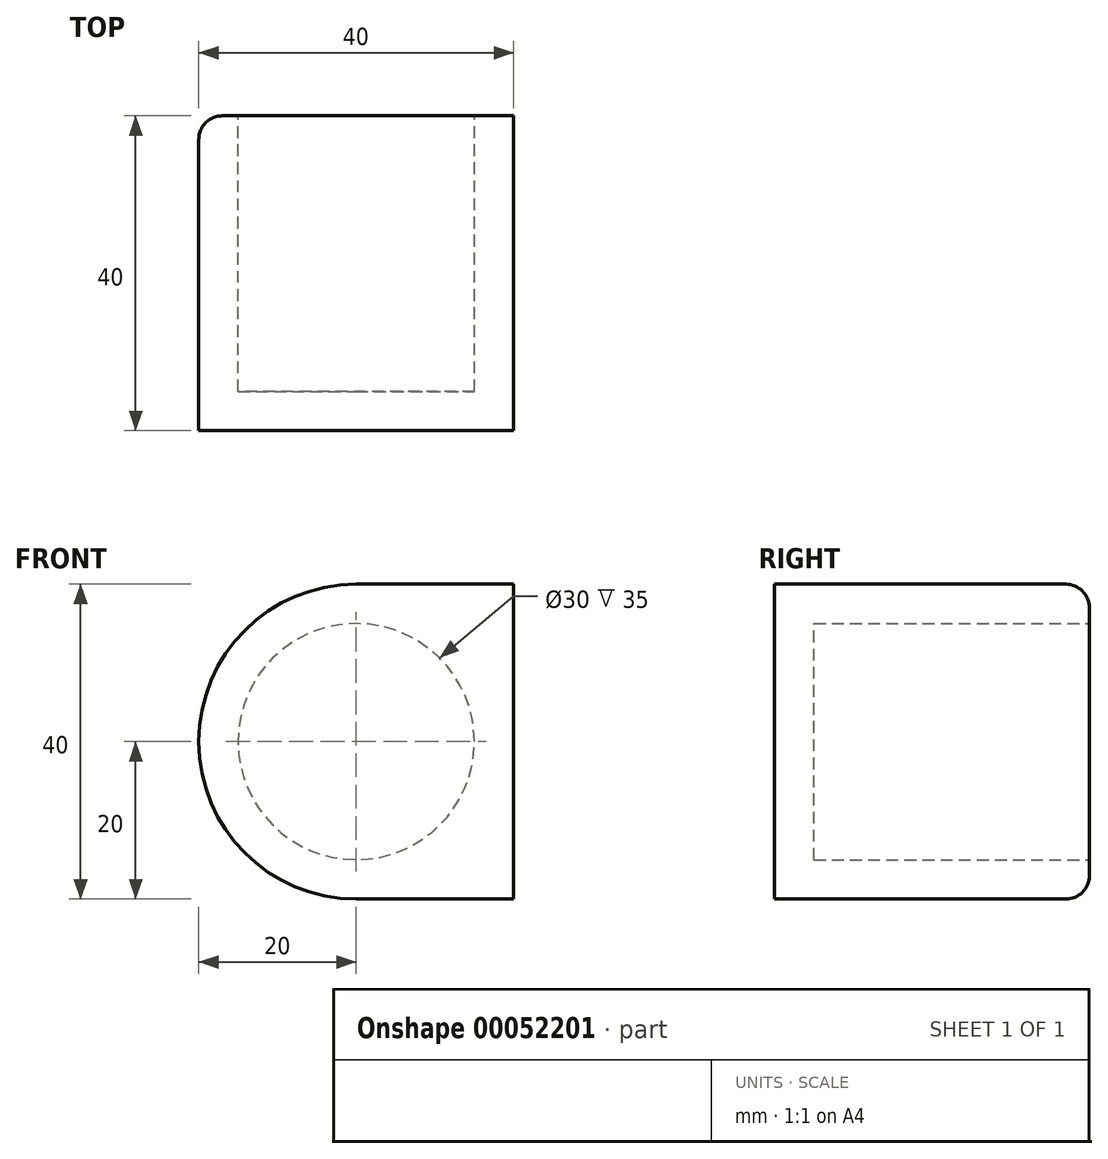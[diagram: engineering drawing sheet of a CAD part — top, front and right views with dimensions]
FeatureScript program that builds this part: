
annotation { "Feature Type Name" : "Feature", "Feature Type Description" : "" }
export const myFeature = defineFeature(function(context is Context, id is Id, definition is map)
    precondition{}
    {
        {
            var Q0;
            Q0=qCreatedBy(makeId("Front.planeOp"),FACE);
            var sketch = newSketch(context, id + "F0", { "sketchPlane" : qUnion([Q0])});
            skLineSegment(sketch, "E0.bottom", {"start": v(0, 0) * mm, "end": v(-40, 0) * mm});
            skLineSegment(sketch, "E0.top", {"start": v(0, -40) * mm, "end": v(-40, -40) * mm});
            skLineSegment(sketch, "E0.left", {"start": v(0, 0) * mm, "end": v(0, -40) * mm});
            skLineSegment(sketch, "E0.right", {"start": v(-40, 0) * mm, "end": v(-40, -40) * mm});
            skCircle(sketch, "E1", {"center": v(-20, -20) * mm, "radius": 15 * mm});
            skSolve(sketch);
        }
        {
            var Q0;
            Q0=makeQuery(id+"F0.imprint","IMPRINT",FACE,{"disambiguationData":[TD([[makeQuery(id+"F0.imprint","IMPRINT",EDGE,{"derivedFrom":sQuery(id+"F0.wireOp",EDGE,"E0.bottom")}),1.0]])]});
            extrude(context, id + "F1", {"entities" : qUnion([Q0]), "depth" : 35 * mm});
        }
        {
            var Q0;
            Q0=makeQuery(id+"F1.opExtrude","CAP_FACE",FACE,{"disambiguationData":[OSD([sQuery(id+"F0.wireOp",EDGE,"E0.bottom"),sQuery(id+"F0.wireOp",EDGE,"E0.top"),sQuery(id+"F0.wireOp",EDGE,"E0.left"),sQuery(id+"F0.wireOp",EDGE,"E0.right"),sQuery(id+"F0.wireOp",EDGE,"E1")])],"isStart":false});
            var sketch = newSketch(context, id + "F2", { "sketchPlane" : qUnion([Q0])});
            skLineSegment(sketch, "E2.bottom", {"start": v(-40, 0) * mm, "end": v(0, 0) * mm});
            skLineSegment(sketch, "E2.top", {"start": v(-40, -40) * mm, "end": v(0, -40) * mm});
            skLineSegment(sketch, "E2.left", {"start": v(-40, 0) * mm, "end": v(-40, -40) * mm});
            skLineSegment(sketch, "E2.right", {"start": v(0, 0) * mm, "end": v(0, -40) * mm});
            skSolve(sketch);
        }
        {
            var Q0;
            Q0=makeQuery(id+"F2.imprint","IMPRINT",FACE,{"disambiguationData":[TD([[makeQuery(id+"F2.imprint","IMPRINT",EDGE,{"derivedFrom":sQuery(id+"F2.wireOp",EDGE,"E2.bottom")}),1.0]])]});
            var Q1;
            Q1=makeQuery(id+"F2.imprint","IMPRINT",FACE,{"disambiguationData":[TD([[makeQuery(id+"F2.imprint","IMPRINT",EDGE,{"derivedFrom":makeQuery(id+"F1.opExtrude","CAP_EDGE",EDGE,{"disambiguationData":[OSD([sQuery(id+"F0.wireOp",EDGE,"E1")])],"isStart":false})}),1.0]])]});
            extrude(context, id + "F3", {"entities" : qUnion([Q0, Q1]), "operationType" : NewBodyOperationType.ADD, "depth" : 5 * mm});
        }
        {
            var Q0;
            Q0=makeQuery(id+"F1.opExtrude","CAP_EDGE",EDGE,{"disambiguationData":[OSD([sQuery(id+"F0.wireOp",EDGE,"E0.bottom")])],"isStart":true});
            var Q1;
            Q1=makeQuery(id+"F1.opExtrude","CAP_EDGE",EDGE,{"disambiguationData":[OSD([sQuery(id+"F0.wireOp",EDGE,"E0.right")])],"isStart":true});
            var Q2;
            Q2=makeQuery(id+"F1.opExtrude","CAP_EDGE",EDGE,{"disambiguationData":[OSD([sQuery(id+"F0.wireOp",EDGE,"E0.top")])],"isStart":true});
            fillet(context, id + "F4", {"entities" : qUnion([Q0, Q1, Q2]), "radius" : 3 * mm, "tangentPropagation" : true, "allowEdgeOverflow" : false});
        }
        {
            var Q0;
            Q0=makeQuery(id+"F3.boolean.opBoolean","MERGE",EDGE,{"derivedFrom":[makeQuery(id+"F1.opExtrude","SWEPT_EDGE",EDGE,{"disambiguationData":[OSD([sQuery(id+"F0.wireOp",EDGE,"E0.top"),sQuery(id+"F0.wireOp",EDGE,"E0.right")])]}),makeQuery(id+"F3.opExtrude","SWEPT_EDGE",EDGE,{"disambiguationData":[OSD([sQuery(id+"F2.wireOp",EDGE,"E2.top"),sQuery(id+"F2.wireOp",EDGE,"E2.left")])]})]});
            var Q1;
            Q1=makeQuery(id+"F3.boolean.opBoolean","MERGE",EDGE,{"derivedFrom":[makeQuery(id+"F1.opExtrude","SWEPT_EDGE",EDGE,{"disambiguationData":[OSD([sQuery(id+"F0.wireOp",EDGE,"E0.bottom"),sQuery(id+"F0.wireOp",EDGE,"E0.right")])]}),makeQuery(id+"F3.opExtrude","SWEPT_EDGE",EDGE,{"disambiguationData":[OSD([sQuery(id+"F2.wireOp",EDGE,"E2.bottom"),sQuery(id+"F2.wireOp",EDGE,"E2.left")])]})]});
            fillet(context, id + "F5", {"entities" : qUnion([Q0, Q1]), "radius" : 20 * mm, "tangentPropagation" : true, "allowEdgeOverflow" : false});
        }
    });
